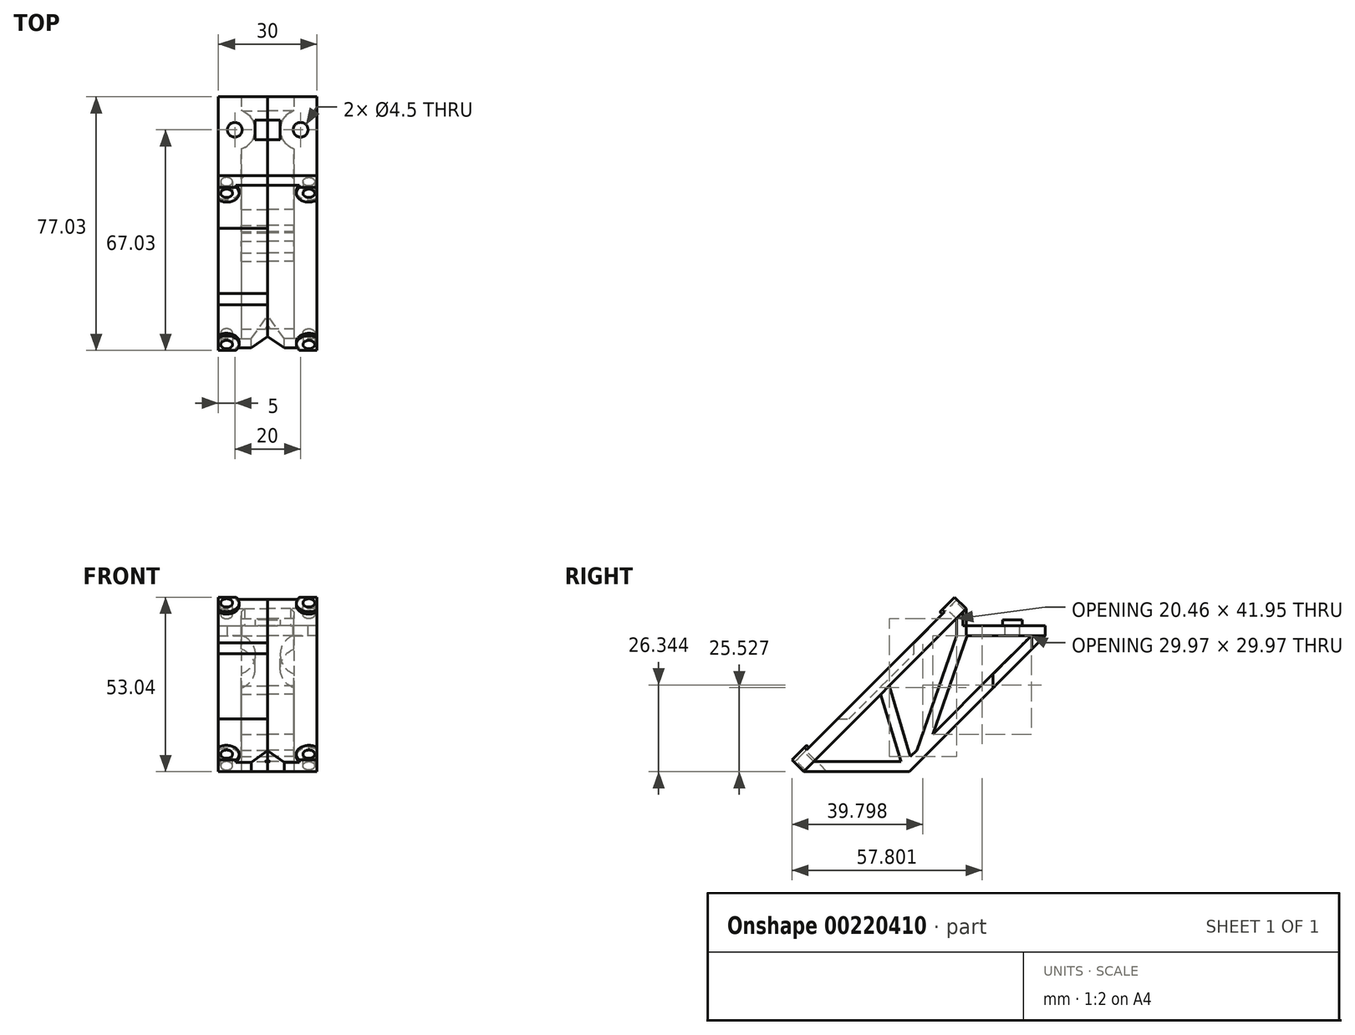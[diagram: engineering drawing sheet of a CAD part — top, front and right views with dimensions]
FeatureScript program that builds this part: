
annotation { "Feature Type Name" : "Feature", "Feature Type Description" : "" }
export const myFeature = defineFeature(function(context is Context, id is Id, definition is map)
    precondition{}
    {
        {
            var Q0;
            Q0=qCreatedBy(makeId("Right.planeOp"),FACE);
            var sketch = newSketch(context, id + "F0", { "sketchPlane" : qUnion([Q0])});
            skLineSegment(sketch, "E0", {"start": v(0, 0) * mm, "end": v(20, 0) * mm});
            skLineSegment(sketch, "E1", {"start": v(-6.83, 8) * mm, "end": v(-56.33, -41.5) * mm});
            skLineSegment(sketch, "E2", {"start": v(0, 0) * mm, "end": v(-4, 0) * mm});
            skLineSegment(sketch, "E3", {"start": v(-6.83, 8) * mm, "end": v(-4, 5.17) * mm});
            skLineSegment(sketch, "E4", {"start": v(-4, 0) * mm, "end": v(-4, 5.17) * mm});
            skLineSegment(sketch, "E5", {"start": v(-4, 5.17) * mm, "end": v(-53.5, -44.33) * mm});
            skLineSegment(sketch, "E6", {"start": v(-53.5, -44.33) * mm, "end": v(-56.33, -41.5) * mm});
            skLineSegment(sketch, "E7", {"start": v(20, 0) * mm, "end": v(20, -3) * mm});
            skLineSegment(sketch, "E8", {"start": v(20, -3) * mm, "end": v(-4, -3) * mm});
            skLineSegment(sketch, "E9", {"start": v(-4, -3) * mm, "end": v(-4, 0) * mm});
            skLineSegment(sketch, "E10", {"start": v(20, -3) * mm, "end": v(-21.33, -44.33) * mm});
            skLineSegment(sketch, "E11", {"start": v(-21.33, -44.33) * mm, "end": v(-53.5, -44.33) * mm});
            skLineSegment(sketch, "E12", {"start": v(-4, -3) * mm, "end": v(-7, -3) * mm});
            skPoint(sketch, "E12.endSnap0", {"position": v(8, -3) * mm});
            skLineSegment(sketch, "E13", {"start": v(-7, -3) * mm, "end": v(-7, 2.17) * mm});
            skLineSegment(sketch, "E14", {"start": v(-21.33, -44.33) * mm, "end": v(-28.75, -19.58) * mm, "construction": true});
            skLineSegment(sketch, "E15", {"start": v(-7, -3) * mm, "end": v(-21.33, -44.33) * mm});
            skLineSegment(sketch, "E16", {"start": v(-3.82, -3) * mm, "end": v(-14.21, -32.97) * mm});
            skLineSegment(sketch, "E17", {"start": v(-14.21, -32.97) * mm, "end": v(15.76, -3) * mm});
            skLineSegment(sketch, "E18", {"start": v(-21.02, -39.78) * mm, "end": v(-27.46, -18.3) * mm});
            skLineSegment(sketch, "E19", {"start": v(-30.03, -20.86) * mm, "end": v(-23.9, -41.33) * mm});
            skLineSegment(sketch, "E20", {"start": v(-23.9, -41.33) * mm, "end": v(-50.5, -41.33) * mm});
            skLineSegment(sketch, "E21", {"start": v(-21.02, -39.78) * mm, "end": v(-19.07, -37.83) * mm});
            skLineSegment(sketch, "E22", {"start": v(-4, 5.17) * mm, "end": v(-18.14, 19.31) * mm, "construction": true});
            skSolve(sketch);
        }
        {
            var Q0;
            Q0=makeQuery(id+"F0.imprint","IMPRINT",FACE,{"disambiguationData":[TD([[makeQuery(id+"F0.imprint","IMPRINT",EDGE,{"derivedFrom":sQuery(id+"F0.wireOp",EDGE,"E1")}),1.0]])]});
            var Q1;
            Q1=makeQuery(id+"F0.imprint","IMPRINT",FACE,{"disambiguationData":[TD([[makeQuery(id+"F0.imprint","IMPRINT",EDGE,{"derivedFrom":sQuery(id+"F0.wireOp",EDGE,"E0")}),-1.0]])]});
            extrude(context, id + "F1", {"entities" : qUnion([Q0, Q1]), "depth" : 15 * mm});
        }
        {
            var Q0;
            {var subQ2=sQuery(id+"F0.wireOp",EDGE,"E10");Q0=makeQuery(id+"F0.imprint","IMPRINT",FACE,{"disambiguationData":[TD([[makeQuery(id+"F0.imprint","IMPRINT",EDGE,{"derivedFrom":subQ2}),-1.0]])]});}
            var Q1;
            {var subQ0=sQuery(id+"F0.wireOp",EDGE,"E11");Q1=makeQuery(id+"F0.imprint","IMPRINT",FACE,{"disambiguationData":[TD([[makeQuery(id+"F0.imprint","IMPRINT",EDGE,{"derivedFrom":subQ0}),-1.0]])]});}
            var Q2;
            {var subQ1=sQuery(id+"F0.wireOp",EDGE,"E4");Q2=makeQuery(id+"F0.imprint","IMPRINT",FACE,{"disambiguationData":[TD([[makeQuery(id+"F0.imprint","IMPRINT",EDGE,{"derivedFrom":subQ1}),1.0]])]});}
            extrude(context, id + "F2", {"entities" : qUnion([Q0, Q1, Q2]), "operationType" : NewBodyOperationType.ADD, "depth" : 8 * mm});
        }
        {
            var Q0;
            Q0=makeQuery(id+"F1.opExtrude","SWEPT_FACE",FACE,{"disambiguationData":[OSD([sQuery(id+"F0.wireOp",EDGE,"E0"),sQuery(id+"F0.wireOp",EDGE,"E2")])]});
            var sketch = newSketch(context, id + "F3", { "sketchPlane" : qUnion([Q0])});
            skCircle(sketch, "E23", {"center": v(10, 10) * mm, "radius": 6.2 * mm});
            skLineSegment(sketch, "E24.bottom", {"start": v(0, 13) * mm, "end": v(3.8, 13) * mm});
            skLineSegment(sketch, "E24.top", {"start": v(0, 7) * mm, "end": v(3.8, 7) * mm});
            skLineSegment(sketch, "E24.left", {"start": v(0, 13) * mm, "end": v(0, 7) * mm});
            skLineSegment(sketch, "E24.right", {"start": v(3.8, 13) * mm, "end": v(3.8, 7) * mm});
            skPoint(sketch, "E24.middle", {"position": v(1.9, 10) * mm});
            skCircle(sketch, "E25", {"center": v(10, 10) * mm, "radius": 2.25 * mm});
            skSolve(sketch);
        }
        {
            var Q0;
            {var subQ1=sQuery(id+"F3.wireOp",EDGE,"E24.bottom");Q0=makeQuery(id+"F3.imprint","IMPRINT",FACE,{"disambiguationData":[TD([[makeQuery(id+"F3.imprint","IMPRINT",EDGE,{"derivedFrom":subQ1}),-1.0]])]});}
            extrude(context, id + "F4", {"entities" : qUnion([Q0]), "operationType" : NewBodyOperationType.ADD, "depth" : 1.8 * mm});
        }
        {
            var Q0;
            Q0=makeQuery(id+"F3.imprint","IMPRINT",FACE,{"disambiguationData":[TD([[makeQuery(id+"F3.imprint","IMPRINT",EDGE,{"derivedFrom":sQuery(id+"F3.wireOp",EDGE,"E25")}),1.0]])]});
            extrude(context, id + "F5", {"entities" : qUnion([Q0]), "operationType" : NewBodyOperationType.REMOVE, "endBound" : BoundingType.THROUGH_ALL, "oppositeDirection" : true, "depth" : 25 * mm});
        }
        {
            var Q0;
            Q0=makeQuery(id+"F3.imprint","IMPRINT",FACE,{"disambiguationData":[TD([[makeQuery(id+"F3.imprint","IMPRINT",EDGE,{"derivedFrom":sQuery(id+"F3.wireOp",EDGE,"E25")}),-1.0]])]});
            var Q1;
            Q1=makeQuery(id+"F1.opExtrude","SWEPT_FACE",FACE,{"disambiguationData":[OSD([sQuery(id+"F0.wireOp",EDGE,"E8")])]});
            extrude(context, id + "F6", {"entities" : qUnion([Q0]), "operationType" : NewBodyOperationType.REMOVE, "endBound" : BoundingType.THROUGH_ALL, "oppositeDirection" : true, "depth" : 25 * mm, "hasSecondDirection" : true, "secondDirectionBound" : SecondDirectionBoundingType.UP_TO_SURFACE, "secondDirectionOppositeDirection" : true, "secondDirectionBoundEntityFace" : qUnion([Q1]), "secondDirectionDepth" : 25 * mm});
        }
        {
            var Q0;
            Q0=makeQuery(id+"F1.opExtrude","SWEPT_FACE",FACE,{"disambiguationData":[OSD([sQuery(id+"F0.wireOp",EDGE,"E1")])]});
            var sketch = newSketch(context, id + "F7", { "sketchPlane" : qUnion([Q0])});
            skCircle(sketch, "E26", {"center": v(12.5, -1.67) * mm, "radius": 1.8 * mm});
            skCircle(sketch, "E27", {"center": v(12.5, -66.67) * mm, "radius": 1.8 * mm});
            skArc(sketch, "E28", {"start": v(9.64, 0.83) * mm, "mid": v(9.81, -4.36) * mm, "end": v(15, -4.53) * mm});
            skArc(sketch, "E29", {"start": v(15, -63.8) * mm, "mid": v(9.81, -63.98) * mm, "end": v(9.64, -69.17) * mm});
            skSolve(sketch);
        }
        {
            var Q0;
            Q0=makeQuery(id+"F7.imprint","IMPRINT",FACE,{"disambiguationData":[TD([[makeQuery(id+"F7.imprint","IMPRINT",EDGE,{"derivedFrom":sQuery(id+"F7.wireOp",EDGE,"E26")}),1.0]])]});
            var Q1;
            Q1=makeQuery(id+"F7.imprint","IMPRINT",FACE,{"disambiguationData":[TD([[makeQuery(id+"F7.imprint","IMPRINT",EDGE,{"derivedFrom":sQuery(id+"F7.wireOp",EDGE,"E27")}),1.0]])]});
            extrude(context, id + "F8", {"entities" : qUnion([Q0, Q1]), "operationType" : NewBodyOperationType.REMOVE, "endBound" : BoundingType.UP_TO_NEXT, "oppositeDirection" : true, "depth" : 25 * mm});
        }
        {
            var Q0;
            Q0=makeQuery(id+"F7.imprint","IMPRINT",FACE,{"disambiguationData":[TD([[makeQuery(id+"F7.imprint","IMPRINT",EDGE,{"derivedFrom":sQuery(id+"F7.wireOp",EDGE,"E26")}),-1.0]])]});
            var Q1;
            Q1=makeQuery(id+"F7.imprint","IMPRINT",FACE,{"disambiguationData":[TD([[makeQuery(id+"F7.imprint","IMPRINT",EDGE,{"derivedFrom":sQuery(id+"F7.wireOp",EDGE,"E27")}),-1.0]])]});
            extrude(context, id + "F9", {"entities" : qUnion([Q0, Q1]), "operationType" : NewBodyOperationType.ADD, "depth" : 1 * mm});
        }
        {
            var Q0;
            Q0=makeQuery(id+"F9.opExtrude","CAP_EDGE",EDGE,{"disambiguationData":[OSD([sQuery(id+"F7.wireOp",EDGE,"E28")])],"isStart":true});
            var Q1;
            Q1=makeQuery(id+"F9.opExtrude","CAP_EDGE",EDGE,{"disambiguationData":[OSD([sQuery(id+"F7.wireOp",EDGE,"E29")])],"isStart":true});
            var Q2;
            {var subQ0=sQuery(id+"F0.wireOp",EDGE,"E9");var subQ1=sQuery(id+"F0.wireOp",EDGE,"E8");var subQ2=sQuery(id+"F0.wireOp",EDGE,"E4");Q2=makeQuery(id+"F2.boolean.opBoolean","SPLIT",EDGE,{"disambiguationData":[TD([makeQuery(id+"F1.opExtrude","SWEPT_FACE",FACE,{"disambiguationData":[OSD([subQ1])]})])],"derivedFrom":makeQuery(id+"F2.opExtrude","CAP_EDGE",EDGE,{"disambiguationData":[OSD([subQ2,subQ0])],"isStart":false})});}
            var Q3;
            {var subQ0=sQuery(id+"F0.wireOp",EDGE,"E5");Q3=makeQuery(id+"F2.opExtrude","CAP_EDGE",EDGE,{"disambiguationData":[OSD([subQ0]),TDD([makeQuery(id+"F0.imprint","IMPRINT",EDGE,{"disambiguationData":[TD([[makeQuery(id+"F0.imprint","INTERSECT",VERTEX,{"derivedFrom":[subQ0,sQuery(id+"F0.wireOp",EDGE,"E18")]}),-1.0]])],"derivedFrom":subQ0})])],"isStart":false});}
            var Q4;
            {var subQ0=sQuery(id+"F0.wireOp",EDGE,"E8");Q4=makeQuery(id+"F2.opExtrude","CAP_EDGE",EDGE,{"disambiguationData":[OSD([subQ0]),TDD([makeQuery(id+"F0.imprint","IMPRINT",EDGE,{"disambiguationData":[TD([[makeQuery(id+"F0.imprint","INTERSECT",VERTEX,{"derivedFrom":[subQ0,sQuery(id+"F0.wireOp",EDGE,"E17")]}),1.0]])],"derivedFrom":subQ0})])],"isStart":false});}
            chamfer(context, id + "F10", {"entities" : qUnion([Q0, Q1, Q2, Q3, Q4]), "width" : 1 * mm, "tangentPropagation" : true});
        }
        {
            var Q0;
            Q0=makeQuery(id+"F1.opExtrude","SWEPT_FACE",FACE,{"disambiguationData":[OSD([sQuery(id+"F0.wireOp",EDGE,"E5")])]});
            var sketch = newSketch(context, id + "F11", { "sketchPlane" : qUnion([Q0])});
            skCircle(sketch, "E30.cCircle", {"center": v(12.5, 1.67) * mm, "radius": 2.85 * mm, "construction": true});
            skLineSegment(sketch, "E30.0", {"start": v(14.15, -1.18) * mm, "end": v(10.85, -1.18) * mm});
            skLineSegment(sketch, "E30.1", {"start": v(10.85, -1.18) * mm, "end": v(9.2, 1.67) * mm});
            skLineSegment(sketch, "E30.2", {"start": v(9.2, 1.67) * mm, "end": v(10.85, 4.52) * mm});
            skLineSegment(sketch, "E30.3", {"start": v(10.85, 4.52) * mm, "end": v(14.15, 4.52) * mm});
            skLineSegment(sketch, "E30.4", {"start": v(14.15, 4.52) * mm, "end": v(15.8, 1.67) * mm});
            skLineSegment(sketch, "E30.5", {"start": v(15.8, 1.67) * mm, "end": v(14.15, -1.18) * mm});
            skPoint(sketch, "E30.0.midPoint", {"position": v(12.5, -1.18) * mm});
            skCircle(sketch, "E31.cCircle", {"center": v(12.5, 66.67) * mm, "radius": 2.85 * mm, "construction": true});
            skLineSegment(sketch, "E31.0", {"start": v(10.85, 69.52) * mm, "end": v(14.15, 69.52) * mm});
            skLineSegment(sketch, "E31.1", {"start": v(14.15, 69.52) * mm, "end": v(15.8, 66.67) * mm});
            skLineSegment(sketch, "E31.2", {"start": v(15.8, 66.67) * mm, "end": v(14.15, 63.82) * mm});
            skLineSegment(sketch, "E31.3", {"start": v(14.15, 63.82) * mm, "end": v(10.85, 63.82) * mm});
            skLineSegment(sketch, "E31.4", {"start": v(10.85, 63.82) * mm, "end": v(9.2, 66.67) * mm});
            skLineSegment(sketch, "E31.5", {"start": v(9.2, 66.67) * mm, "end": v(10.85, 69.52) * mm});
            skPoint(sketch, "E31.0.midPoint", {"position": v(12.5, 69.52) * mm});
            skSolve(sketch);
        }
        {
            var Q0;
            {var subQ10=sQuery(id+"F11.wireOp",EDGE,"E30.2");Q0=makeQuery(id+"F11.imprint","IMPRINT",FACE,{"disambiguationData":[TD([[makeQuery(id+"F11.imprint","IMPRINT",EDGE,{"derivedFrom":subQ10}),-1.0]])]});}
            var Q1;
            {var subQ7=sQuery(id+"F11.wireOp",EDGE,"E31.3");Q1=makeQuery(id+"F11.imprint","IMPRINT",FACE,{"disambiguationData":[TD([[makeQuery(id+"F11.imprint","IMPRINT",EDGE,{"derivedFrom":subQ7}),-1.0]])]});}
            var Q2;
            {var subQ0=sQuery(id+"F11.wireOp",EDGE,"E31.1");var subQ1=sQuery(id+"F0.wireOp",EDGE,"E5");var subQ4=makeQuery(id+"F1.opExtrude","CAP_EDGE",EDGE,{"disambiguationData":[OSD([subQ1])],"isStart":false});var subQ5=makeQuery(id+"F11.imprint","INTERSECT",VERTEX,{"derivedFrom":[subQ4,subQ0]});Q2=makeQuery(id+"F11.imprint","IMPRINT",FACE,{"disambiguationData":[TD([[makeQuery(id+"F11.imprint","IMPRINT",EDGE,{"disambiguationData":[TD([[subQ5,1.0]])],"derivedFrom":subQ0}),1.0]])]});}
            var Q3;
            {var subQ0=sQuery(id+"F11.wireOp",EDGE,"E30.5");var subQ1=sQuery(id+"F0.wireOp",EDGE,"E5");var subQ2=makeQuery(id+"F1.opExtrude","CAP_EDGE",EDGE,{"disambiguationData":[OSD([subQ1])],"isStart":false});var subQ3=makeQuery(id+"F11.imprint","INTERSECT",VERTEX,{"derivedFrom":[subQ2,subQ0]});Q3=makeQuery(id+"F11.imprint","IMPRINT",FACE,{"disambiguationData":[TD([[makeQuery(id+"F11.imprint","IMPRINT",EDGE,{"disambiguationData":[TD([[subQ3,-1.0]])],"derivedFrom":subQ0}),1.0]])]});}
            extrude(context, id + "F12", {"entities" : qUnion([Q0, Q1, Q2, Q3]), "operationType" : NewBodyOperationType.REMOVE, "oppositeDirection" : true, "depth" : 2 * mm});
        }
        {
            var Q0;
            Q0=makeQuery(id+"F1.opExtrude","CAP_EDGE",EDGE,{"disambiguationData":[OSD([sQuery(id+"F0.wireOp",EDGE,"E6")])],"isStart":true});
            chamfer(context, id + "F13", {"entities" : qUnion([Q0]), "width" : 5 * mm, "tangentPropagation" : true});
        }
        {
            var Q0;
            Q0=makeQuery(id+"F1.opExtrude","SWEPT_BODY",BODY,{"disambiguationData":[OSD([sQuery(id+"F0.wireOp",EDGE,"E0"),sQuery(id+"F0.wireOp",EDGE,"E2"),sQuery(id+"F0.wireOp",EDGE,"E7"),sQuery(id+"F0.wireOp",EDGE,"E8"),sQuery(id+"F0.wireOp",EDGE,"E9")])]});
            var Q1;
            Q1=qCreatedBy(makeId("Right.planeOp"),FACE);
            mirror(context, id + "F14", {"entities" : qUnion([Q0]), "mirrorPlane" : qUnion([Q1])});
        }
        {
            var Q0;
            {var subQ0=sQuery(id+"F0.wireOp",EDGE,"E1");var subQ1=makeQuery(id+"F1.opExtrude","CAP_EDGE",EDGE,{"disambiguationData":[OSD([subQ0])],"isStart":false});var subQ2=sQuery(id+"F0.wireOp",EDGE,"E6");var subQ3=sQuery(id+"F0.wireOp",EDGE,"E3");Q0=makeQuery(id+"F14.opPattern","COPY",FACE,{"derivedFrom":makeQuery(id+"F9.boolean.opBoolean","MERGE",FACE,{"derivedFrom":[makeQuery(id+"F1.opExtrude","CAP_FACE",FACE,{"disambiguationData":[OSD([subQ0,subQ3,sQuery(id+"F0.wireOp",EDGE,"E5"),subQ2])],"isStart":false}),makeQuery(id+"F9.opExtrude","SWEPT_FACE",FACE,{"disambiguationData":[OSD([subQ0]),TDD([makeQuery(id+"F7.imprint","IMPRINT",EDGE,{"disambiguationData":[TD([[makeQuery(id+"F7.imprint","INTERSECT",VERTEX,{"derivedFrom":[subQ1,sQuery(id+"F7.wireOp",EDGE,"E28")]}),1.0]])],"derivedFrom":subQ1})])]}),makeQuery(id+"F9.opExtrude","SWEPT_FACE",FACE,{"disambiguationData":[OSD([subQ0]),TDD([makeQuery(id+"F7.imprint","IMPRINT",EDGE,{"disambiguationData":[TD([[makeQuery(id+"F7.imprint","INTERSECT",VERTEX,{"derivedFrom":[subQ1,sQuery(id+"F7.wireOp",EDGE,"E29")]}),-1.0]])],"derivedFrom":subQ1})])]})]}),"instanceName":"1"});}
            var sketch = newSketch(context, id + "F15", { "sketchPlane" : qUnion([Q0])});
            skLineSegment(sketch, "E32", {"start": v(19.98, -5.15) * mm, "end": v(19.98, -8.55) * mm});
            skLineSegment(sketch, "E33", {"start": v(19.98, -8.55) * mm, "end": v(39.78, -28.35) * mm});
            skLineSegment(sketch, "E34", {"start": v(39.78, -28.35) * mm, "end": v(43.17, -28.35) * mm});
            skSolve(sketch);
        }
        {
            var Q0;
            {var subQ0=sQuery(id+"F15.wireOp",EDGE,"E32");Q0=makeQuery(id+"F15.imprint","IMPRINT",FACE,{"disambiguationData":[TD([[makeQuery(id+"F15.imprint","IMPRINT",EDGE,{"derivedFrom":subQ0}),1.0]])]});}
            extrude(context, id + "F16", {"entities" : qUnion([Q0]), "operationType" : NewBodyOperationType.REMOVE, "endBound" : BoundingType.UP_TO_NEXT, "oppositeDirection" : true, "depth" : 25 * mm});
        }
    });
